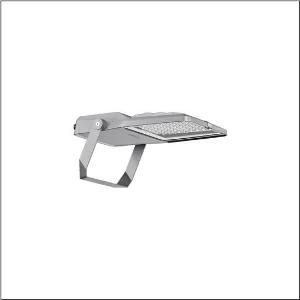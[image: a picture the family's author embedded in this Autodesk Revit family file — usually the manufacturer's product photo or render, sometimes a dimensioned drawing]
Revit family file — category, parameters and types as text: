
# Revit family: floodlight_fl_21_iq_mini___pl61_5xa7772d4c1a_f35a
name_source: partatom
category: Lighting Fixtures
units: mm (PartAtom-declared; Revit-internal decimal feet)

## family parameters
Cut with Voids When Loaded = No
Host = Face
Light Source = No
Part Type = Normal
Room Calculation Point = No
Round Connector Dimension = Use Diameter
Shared = No

## types (1)
- --- (1 x LED, 18260 lm, 143 W, 4000K)
    Apparent Load = 143 VA
    CIE Flux Codes = 33 65 98 100 100
    Color Rendering = 70
    Color Temperature = 4000K
    Default Elevation = 1800 mm
    Description = Floodlight FL 21 iQ mini, floodlight, primary light control with lens, of PMMA, primary optical cover: protective disc, of toughened safety glass, transparent, light distribution: PL61, light emission: direct distribution, installation type: surface-mounted, LED, High Power LED, rated luminous flux: 18.260lm, luminous efficacy: 128lm/W, light colour: 740, colour temperature: 4000K, control: Street-Remote, Auto-Match, Temp-Guard, Night-Set, Smart-Wire, Desk-Remote (wireless, voltage-free reading and setting of iQ features in the workshop via application-optimized NFC function/RFID function), optimised constant luminous flux control (CLO 2.0), with terminal, 6-pole, mains connection: 220..240V, AC, 50/60Hz, start of lifetime: 143W, end of service life: 152W, reduction: 61W, luminaire housing, of diecast aluminium, powder-coated, Siteco® metallic grey (DB 702S), corrosivity category C5 mid according to DIN EN ISO 12944, sealing non-destructively replaceable, mounting bracket, of steel, galvanised, powder-coated, Siteco® metallic grey (DB 702S), protection rating (complete): IP66, insulation class (complete): insulation class II (safety insulation), certification: CE, ENEC, VDE, protection symbol: D, impact resistance: IK08, permissible operating ambient temperature: -40..+40°C, permissible operating ambient temperature for outdoor applications: -40..+50°C, standard: DIN EN 12944, LABS conformity tested according to VDMA 24364:2018-05, packaging unit: 1 piece

Light Distribution: PL61
    Height = 70 mm
    Lamp = 1 x LED
    Lamp Light Flux = 18260 lm
    Lamp Power = 143 W
    Lamp count = 1
    Length = 485 mm
    Luminous efficacy = 128 lm/W
    Manufacturer = Siteco
    ModVariant = No
    Model = 5XA7772D4C1A
    Number of Poles = 1
    OnlyDefault = Yes
    Power Factor = 1
    Product Name = Floodlight FL 21 iQ mini | PL61
    Product group = floodlight | pylon annexe
    ProductGroupID = 6200
    Protection Class = Protection class II
    Protection Degree = IP 66
    RLX_Detail_Level = 1
    RLX_Emergency_Light_Flux = 0 lm
    RLX_Emergency_Type = 0
    RLX_Emergency_Type_DB = No
    RlxData = <blob elided: 96569 chars, md5=981f0e3f>
    Socket = socket
    Standby Power = 0 W
    System Light Flux = 18260 lm
    System Power = 143 W
    Type Comments = factory setting: luminous flux: 100 % | dim-lin: 254 | 730 mA
    Type Image = l_1006845.jpg
    URL = http://relux.com
    VarID = @adj_105451
    Voltage = 0 V
    Weight = 0.00 kg
    Width = 337 mm

## geometry (parser evidence)
native form markers: Blend x4, Sweep x13
no freeform markers — native parametric forms only
